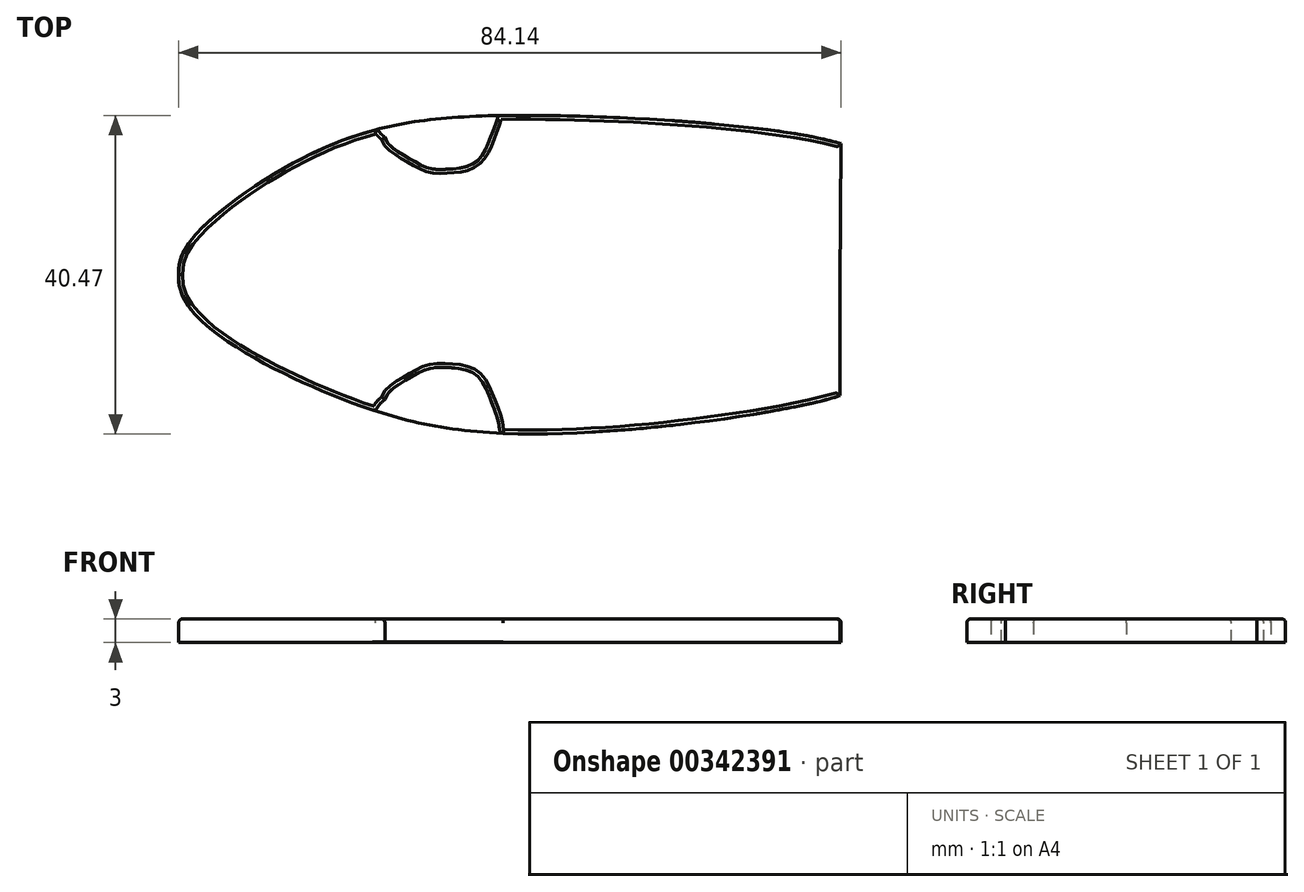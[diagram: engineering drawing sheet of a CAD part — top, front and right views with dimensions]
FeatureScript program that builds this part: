
annotation { "Feature Type Name" : "Feature", "Feature Type Description" : "" }
export const myFeature = defineFeature(function(context is Context, id is Id, definition is map)
    precondition{}
    {
        {
            var Q0;
            Q0=qCreatedBy(makeId("Top.planeOp"),FACE);
            var sketch = newSketch(context, id + "F0", { "sketchPlane" : qUnion([Q0])});
            skFitSpline(sketch, "E0", {"points": [v(38.67, 18.02) * mm, v(-1.71, 21.63) * mm, v(-25.73, 18.02) * mm, v(-42.02, 7.78) * mm, v(-45.45, 1.4) * mm], "startDerivative": vector(-64.35, 20.1) * mm, "endDerivative": vector(4.54, -45.94) * mm});
            skLineSegment(sketch, "E1", {"start": v(38.67, 18.02) * mm, "end": v(38.55, 3.02) * mm});
            skLineSegment(sketch, "E2.left", {"start": v(38.67, 18.02) * mm, "end": v(38.55, 0.17) * mm});
            skFitSpline(sketch, "E3.MirrorCS", {"points": [v(38.55, -13.98) * mm, v(-1.71, -18.83) * mm, v(-25.73, -13.98) * mm, v(-42.02, -4.98) * mm, v(-45.45, 1.4) * mm], "startDerivative": vector(-64.35, -20.1) * mm, "endDerivative": vector(4.54, 45.94) * mm});
            skLineSegment(sketch, "E4.MirrorCS", {"start": v(38.55, -13.98) * mm, "end": v(38.55, 0.17) * mm});
            skSolve(sketch);
        }
        {
            var Q0;
            Q0 = qSketchRegion(id + "F0", true);
            extrude(context, id + "F1", {"entities" : qUnion([Q0]), "depth" : 3 * mm});
        }
        {
            var Q0;
            Q0=qCreatedBy(makeId("Top.planeOp"),FACE);
            cPlane(context, id + "F2", {"entities" : qUnion([Q0]), "cplaneType" : CPlaneType.OFFSET, "offset" : 3 * mm, "width" : 150 * mm, "height" : 150 * mm});
        }
        {
            var Q0;
            Q0=qCreatedBy(id+"F2.planeOp",FACE);
            var sketch = newSketch(context, id + "F3", { "sketchPlane" : qUnion([Q0])});
            skFitSpline(sketch, "E5", {"points": [v(-19.26, -14.48) * mm, v(-16.15, -11.75) * mm, v(-13.67, -10.53) * mm, v(-11.32, -10.4) * mm, v(-7.74, -11.29) * mm, v(-5.72, -14.8) * mm, v(-4.73, -18.8) * mm], "startDerivative": vector(2.76, 17.96) * mm, "endDerivative": vector(-1.93, -21.6) * mm});
            skFitSpline(sketch, "E6", {"points": [v(-19.26, -14.48) * mm, v(-20.56, -17.38) * mm, v(-14.66, -18.13) * mm, v(-12.38, -19.38) * mm, v(-10.82, -18.55) * mm, v(-9.07, -19.09) * mm, v(-8.63, -19.14) * mm, v(-4.73, -18.8) * mm], "startDerivative": vector(-16.46, -9.88) * mm, "endDerivative": vector(0.77, 26.85) * mm});
            skPoint(sketch, "E7.endSnap0", {"position": v(38.7, 2.2) * mm});
            skLineSegment(sketch, "E8", {"start": v(38.7, 2.2) * mm, "end": v(-62.32, 2.2) * mm});
            skFitSpline(sketch, "E9.MirrorCS", {"points": [v(-19.26, 18.86) * mm, v(-16.15, 16.13) * mm, v(-13.67, 14.92) * mm, v(-11.32, 14.8) * mm, v(-7.74, 15.68) * mm, v(-5.72, 19.18) * mm, v(-4.73, 23.18) * mm], "startDerivative": vector(2.76, -17.96) * mm, "endDerivative": vector(-1.93, 21.6) * mm});
            skFitSpline(sketch, "E10.MirrorCS", {"points": [v(-19.26, 18.86) * mm, v(-20.56, 21.76) * mm, v(-14.66, 22.52) * mm, v(-12.38, 23.77) * mm, v(-10.82, 22.93) * mm, v(-9.07, 23.48) * mm, v(-8.63, 23.52) * mm, v(-4.73, 23.18) * mm], "startDerivative": vector(-16.46, 9.88) * mm, "endDerivative": vector(0.77, -26.85) * mm});
            skSolve(sketch);
        }
        {
            var Q0;
            Q0 = qSketchRegion(id + "F3", true);
            extrude(context, id + "F4", {"entities" : qUnion([Q0]), "operationType" : NewBodyOperationType.REMOVE, "oppositeDirection" : true, "depth" : 2.9 * mm});
        }
        {
            var Q0;
            {var subQ0=sQuery(id+"F0.wireOp",EDGE,"E0");var subQ1=sQuery(id+"F0.wireOp",EDGE,"E3.MirrorCS");Q0=makeQuery(id+"F4.boolean.opBoolean","SPLIT",EDGE,{"disambiguationData":[TD([makeQuery(id+"F1.opExtrude","SWEPT_FACE",FACE,{"disambiguationData":[OSD([subQ0])]})])],"derivedFrom":makeQuery(id+"F1.opExtrude","CAP_EDGE",EDGE,{"disambiguationData":[OSD([subQ1])],"isStart":false})});}
            var Q1;
            {var subQ0=sQuery(id+"F0.wireOp",EDGE,"E0");var subQ1=sQuery(id+"F0.wireOp",EDGE,"E3.MirrorCS");Q1=makeQuery(id+"F4.boolean.opBoolean","SPLIT",EDGE,{"disambiguationData":[TD([makeQuery(id+"F1.opExtrude","SWEPT_FACE",FACE,{"disambiguationData":[OSD([subQ1])]})])],"derivedFrom":makeQuery(id+"F1.opExtrude","CAP_EDGE",EDGE,{"disambiguationData":[OSD([subQ0])],"isStart":false})});}
            var Q2;
            {var subQ0=sQuery(id+"F0.wireOp",EDGE,"E0");var subQ1=sQuery(id+"F0.wireOp",EDGE,"E2.left");Q2=makeQuery(id+"F4.boolean.opBoolean","SPLIT",EDGE,{"disambiguationData":[TD([makeQuery(id+"F1.opExtrude","SWEPT_FACE",FACE,{"disambiguationData":[OSD([subQ1])]})])],"derivedFrom":makeQuery(id+"F1.opExtrude","CAP_EDGE",EDGE,{"disambiguationData":[OSD([subQ0])],"isStart":false})});}
            var Q3;
            {var subQ0=sQuery(id+"F0.wireOp",EDGE,"E4.MirrorCS");var subQ1=sQuery(id+"F0.wireOp",EDGE,"E3.MirrorCS");Q3=makeQuery(id+"F4.boolean.opBoolean","SPLIT",EDGE,{"disambiguationData":[TD([makeQuery(id+"F1.opExtrude","SWEPT_FACE",FACE,{"disambiguationData":[OSD([subQ0])]})])],"derivedFrom":makeQuery(id+"F1.opExtrude","CAP_EDGE",EDGE,{"disambiguationData":[OSD([subQ1])],"isStart":false})});}
            var Q4;
            Q4=makeQuery(id+"F1.opExtrude","CAP_EDGE",EDGE,{"disambiguationData":[OSD([sQuery(id+"F0.wireOp",EDGE,"E4.MirrorCS")])],"isStart":false});
            var Q5;
            Q5=makeQuery(id+"F1.opExtrude","CAP_EDGE",EDGE,{"disambiguationData":[OSD([sQuery(id+"F0.wireOp",EDGE,"E2.left")])],"isStart":false});
            fillet(context, id + "F5", {"entities" : qUnion([Q0, Q1, Q2, Q3, Q4, Q5]), "radius" : 0.5 * mm, "tangentPropagation" : true, "allowEdgeOverflow" : false});
        }
        {
            var Q0;
            Q0=makeQuery(id+"F4.boolean.opBoolean","INTERSECT",EDGE,{"derivedFrom":[makeQuery(id+"F1.opExtrude","SWEPT_FACE",FACE,{"disambiguationData":[OSD([sQuery(id+"F0.wireOp",EDGE,"E3.MirrorCS")])]}),makeQuery(id+"F4.opExtrude","SWEPT_FACE",FACE,{"disambiguationData":[OSD([sQuery(id+"F3.wireOp",EDGE,"E6")])]})]});
            var Q1;
            Q1=makeQuery(id+"F4.boolean.opBoolean","INTERSECT",EDGE,{"derivedFrom":[makeQuery(id+"F1.opExtrude","SWEPT_FACE",FACE,{"disambiguationData":[OSD([sQuery(id+"F0.wireOp",EDGE,"E3.MirrorCS")])]}),makeQuery(id+"F4.opExtrude","SWEPT_FACE",FACE,{"disambiguationData":[OSD([sQuery(id+"F3.wireOp",EDGE,"E5")])]})]});
            var Q2;
            Q2=makeQuery(id+"F4.boolean.opBoolean","INTERSECT",EDGE,{"derivedFrom":[makeQuery(id+"F1.opExtrude","SWEPT_FACE",FACE,{"disambiguationData":[OSD([sQuery(id+"F0.wireOp",EDGE,"E0")])]}),makeQuery(id+"F4.opExtrude","SWEPT_FACE",FACE,{"disambiguationData":[OSD([sQuery(id+"F3.wireOp",EDGE,"E10.MirrorCS")])]})]});
            var Q3;
            Q3=makeQuery(id+"F4.boolean.opBoolean","INTERSECT",EDGE,{"derivedFrom":[makeQuery(id+"F1.opExtrude","SWEPT_FACE",FACE,{"disambiguationData":[OSD([sQuery(id+"F0.wireOp",EDGE,"E0")])]}),makeQuery(id+"F4.opExtrude","SWEPT_FACE",FACE,{"disambiguationData":[OSD([sQuery(id+"F3.wireOp",EDGE,"E9.MirrorCS")])]})]});
            fillet(context, id + "F6", {"entities" : qUnion([Q0, Q1, Q2, Q3]), "radius" : 0.5 * mm, "tangentPropagation" : true, "allowEdgeOverflow" : false});
        }
    });
